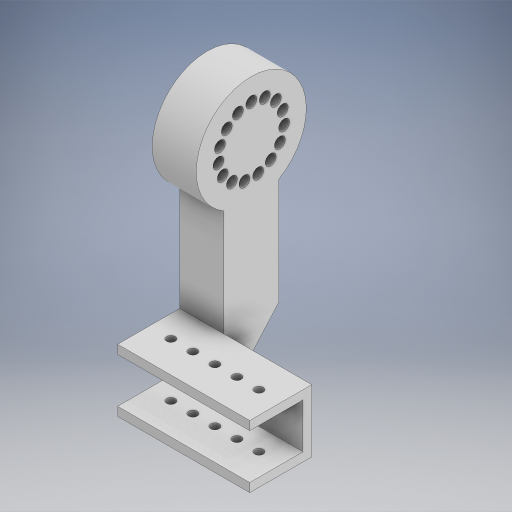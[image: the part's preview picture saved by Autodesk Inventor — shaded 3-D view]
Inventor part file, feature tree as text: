
AUTODESK INVENTOR PART (.ipt)
format: ipt  version: 2024.2 (Build 282272000, 272)  size: 393,216 bytes
history: native  units: in
note: dims shown in document units (in); Inventor stores cm internally (conversion verified against a paired STEP export)
features: extrude x6, sketch x6, projected_geometry x3
ambient origin geometry x8: Origin, YZ Plane, XZ Plane, XY Plane, X Axis, Y Axis, Z Axis, Center Point
bodies: Solid1 (feature_tree)
feature tree (15):
  extrude  "Extrusion1"  Depth=3.0in
  extrude  "Extrusion6"  Depth=0.5in
  extrude  "Extrusion7"  Depth=1.0in
  extrude  "Extrusion8"  Depth=2.625in TaperAngle=0.0deg
  extrude  "Extrusion9"  Depth=1.0in TaperAngle=0.0deg
  extrude  "Extrusion10"  Depth=1.0in
  sketch  "Sketch1"  dims[d6=3.0in d7=0.0in d11=0.196in]
  sketch  "Sketch3"  dims[d13=0.5in d14=0.5in]
  sketch  "Sketch6"  dims[d15=1.5748in d17=0.5in d18=0.3937in d20=1.0in d36=0.196in]
  sketch  "Sketch7"  dims[d37=0.5in d38=2.625in d39=0.0in]
  projected_geometry  "Projected Loop2"
  sketch  "Sketch8"  dims[d40=1.25in d41=1.0in d42=0.0in]
  projected_geometry  "Projected Loop3"
  sketch  "Sketch9"  dims[d43=3.5in d44=0.0in d45=2.5in d46=0.0in d47=0.0in d48=1.5in d49=0.25in d50=5.9055in d52=360.0deg d54=1.0in d55=0.0in d8=0.0in d9=0.0in d10=0.0in]
  projected_geometry  "Projected Loop4"
